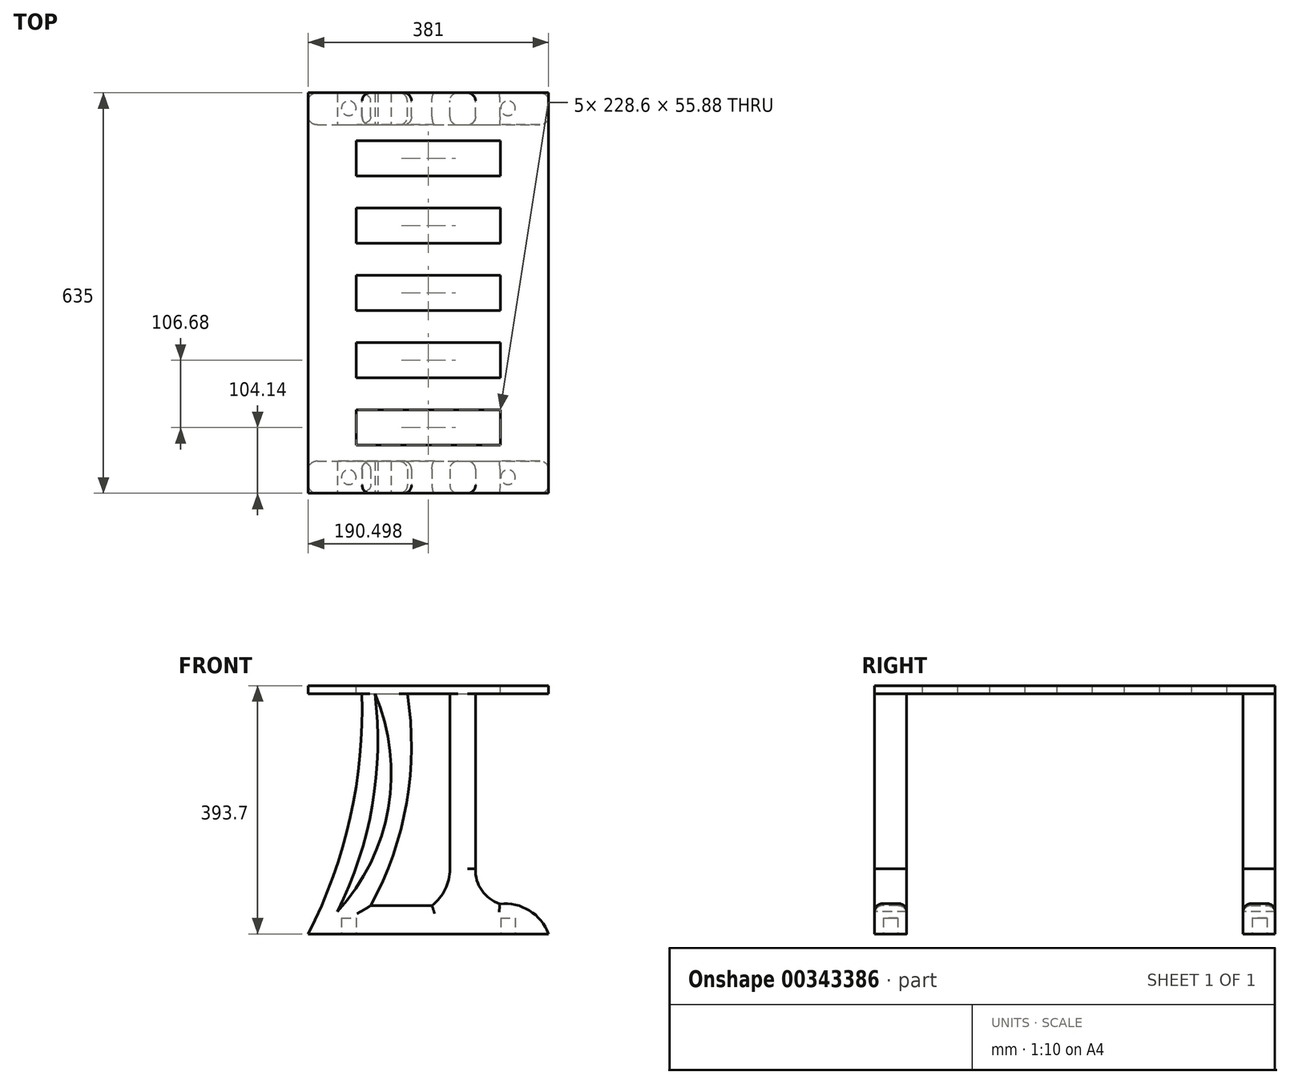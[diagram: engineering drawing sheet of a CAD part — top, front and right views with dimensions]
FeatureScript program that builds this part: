
annotation { "Feature Type Name" : "Feature", "Feature Type Description" : "" }
export const myFeature = defineFeature(function(context is Context, id is Id, definition is map)
    precondition{}
    {
        {
            var Q0;
            Q0=qCreatedBy(makeId("Front.planeOp"),FACE);
            var sketch = newSketch(context, id + "F0", { "sketchPlane" : qUnion([Q0])});
            skArc(sketch, "E0", {"start": v(156.47, -381) * mm, "mid": v(126, -343.99) * mm, "end": v(79.24, -333.37) * mm});
            skArc(sketch, "E1", {"start": v(40.62, -278.03) * mm, "mid": v(50.62, -312.2) * mm, "end": v(79.24, -333.37) * mm});
            skLineSegment(sketch, "E2", {"start": v(40.62, -278.03) * mm, "end": v(40.62, 0) * mm});
            skLineSegment(sketch, "E3", {"start": v(0, 0) * mm, "end": v(0, -278.03) * mm});
            skArc(sketch, "E4", {"start": v(-28.4, -336.03) * mm, "mid": v(-7.48, -310.31) * mm, "end": v(0, -278.03) * mm});
            skArc(sketch, "E5", {"start": v(-224.53, -381) * mm, "mid": v(-157.8, -195.9) * mm, "end": v(-139.58, 0) * mm});
            skLineSegment(sketch, "E6", {"start": v(-224.53, -381) * mm, "end": v(156.47, -381) * mm});
            skLineSegment(sketch, "E7", {"start": v(-139.58, 0) * mm, "end": v(-67.5, 0) * mm});
            skLineSegment(sketch, "E8", {"start": v(0, 0) * mm, "end": v(40.62, 0) * mm});
            skArc(sketch, "E9", {"start": v(-125.38, -336.03) * mm, "mid": v(-68.53, -172.82) * mm, "end": v(-67.5, 0) * mm});
            skLineSegment(sketch, "E10", {"start": v(-28.4, -336.03) * mm, "end": v(-125.38, -336.03) * mm});
            skSolve(sketch);
        }
        {
            var Q0;
            Q0=makeQuery(id+"F0.imprint","IMPRINT",FACE,{"disambiguationData":[TD([[makeQuery(id+"F0.imprint","IMPRINT",EDGE,{"derivedFrom":sQuery(id+"F0.wireOp",EDGE,"E0")}),1.0]])]});
            extrude(context, id + "F1", {"entities" : qUnion([Q0]), "depth" : 50.8 * mm});
        }
        {
            var Q0;
            Q0=qCreatedBy(makeId("Front.planeOp"),FACE);
            var sketch = newSketch(context, id + "F2", { "sketchPlane" : qUnion([Q0])});
            skLineSegment(sketch, "E11", {"start": v(-224.53, 0) * mm, "end": v(156.47, 0) * mm});
            skLineSegment(sketch, "E12", {"start": v(-224.53, 0) * mm, "end": v(-224.53, 12.7) * mm});
            skLineSegment(sketch, "E13", {"start": v(-224.53, 12.7) * mm, "end": v(156.47, 12.7) * mm});
            skLineSegment(sketch, "E14", {"start": v(156.47, 12.7) * mm, "end": v(156.47, 0) * mm});
            skSolve(sketch);
        }
        {
            var Q0;
            Q0=makeQuery(id+"F2.imprint","IMPRINT",FACE,{"disambiguationData":[TD([[makeQuery(id+"F2.imprint","IMPRINT",EDGE,{"derivedFrom":sQuery(id+"F2.wireOp",EDGE,"E11")}),1.0]])]});
            extrude(context, id + "F3", {"entities" : qUnion([Q0]), "operationType" : NewBodyOperationType.ADD, "depth" : 317.5 * mm});
        }
        {
            var Q0;
            Q0=makeQuery(id+"F1.opExtrude","CAP_EDGE",EDGE,{"disambiguationData":[OSD([sQuery(id+"F0.wireOp",EDGE,"E1")])],"isStart":true});
            var Q1;
            Q1=makeQuery(id+"F1.opExtrude","CAP_EDGE",EDGE,{"disambiguationData":[OSD([sQuery(id+"F0.wireOp",EDGE,"E1")])],"isStart":false});
            var Q2;
            Q2=makeQuery(id+"F1.opExtrude","CAP_EDGE",EDGE,{"disambiguationData":[OSD([sQuery(id+"F0.wireOp",EDGE,"E0")])],"isStart":true});
            var Q3;
            Q3=makeQuery(id+"F1.opExtrude","CAP_EDGE",EDGE,{"disambiguationData":[OSD([sQuery(id+"F0.wireOp",EDGE,"E0")])],"isStart":false});
            var Q4;
            Q4=makeQuery(id+"F1.opExtrude","CAP_EDGE",EDGE,{"disambiguationData":[OSD([sQuery(id+"F0.wireOp",EDGE,"E2")])],"isStart":true});
            var Q5;
            Q5=makeQuery(id+"F1.opExtrude","CAP_EDGE",EDGE,{"disambiguationData":[OSD([sQuery(id+"F0.wireOp",EDGE,"E2")])],"isStart":false});
            fillet(context, id + "F4", {"entities" : qUnion([Q0, Q1, Q2, Q3, Q4, Q5]), "radius" : 12.7 * mm, "tangentPropagation" : true, "allowEdgeOverflow" : false});
        }
        {
            var Q0;
            Q0=makeQuery(id+"F1.opExtrude","CAP_EDGE",EDGE,{"disambiguationData":[OSD([sQuery(id+"F0.wireOp",EDGE,"E3")])],"isStart":true});
            var Q1;
            Q1=makeQuery(id+"F1.opExtrude","CAP_EDGE",EDGE,{"disambiguationData":[OSD([sQuery(id+"F0.wireOp",EDGE,"E3")])],"isStart":false});
            var Q2;
            Q2=makeQuery(id+"F1.opExtrude","CAP_EDGE",EDGE,{"disambiguationData":[OSD([sQuery(id+"F0.wireOp",EDGE,"E10")])],"isStart":false});
            var Q3;
            Q3=makeQuery(id+"F1.opExtrude","CAP_EDGE",EDGE,{"disambiguationData":[OSD([sQuery(id+"F0.wireOp",EDGE,"E10")])],"isStart":true});
            var Q4;
            Q4=makeQuery(id+"F1.opExtrude","CAP_EDGE",EDGE,{"disambiguationData":[OSD([sQuery(id+"F0.wireOp",EDGE,"E9")])],"isStart":true});
            var Q5;
            Q5=makeQuery(id+"F1.opExtrude","CAP_EDGE",EDGE,{"disambiguationData":[OSD([sQuery(id+"F0.wireOp",EDGE,"E9")])],"isStart":false});
            var Q6;
            Q6=makeQuery(id+"F1.opExtrude","CAP_EDGE",EDGE,{"disambiguationData":[OSD([sQuery(id+"F0.wireOp",EDGE,"E5")])],"isStart":false});
            var Q7;
            Q7=makeQuery(id+"F1.opExtrude","CAP_EDGE",EDGE,{"disambiguationData":[OSD([sQuery(id+"F0.wireOp",EDGE,"E5")])],"isStart":true});
            fillet(context, id + "F5", {"entities" : qUnion([Q0, Q1, Q2, Q3, Q4, Q5, Q6, Q7]), "radius" : 12.7 * mm, "tangentPropagation" : true, "allowEdgeOverflow" : false});
        }
        {
            var Q0;
            Q0=makeQuery(id+"F1.opExtrude","SWEPT_BODY",BODY,{"disambiguationData":[OSD([sQuery(id+"F0.wireOp",EDGE,"E0"),sQuery(id+"F0.wireOp",EDGE,"E1"),sQuery(id+"F0.wireOp",EDGE,"E2"),sQuery(id+"F0.wireOp",EDGE,"E3"),sQuery(id+"F0.wireOp",EDGE,"E4"),sQuery(id+"F0.wireOp",EDGE,"E5"),sQuery(id+"F0.wireOp",EDGE,"E6"),sQuery(id+"F0.wireOp",EDGE,"E7"),sQuery(id+"F0.wireOp",EDGE,"E8"),sQuery(id+"F0.wireOp",EDGE,"E9"),sQuery(id+"F0.wireOp",EDGE,"E10")])]});
            var Q1;
            Q1=makeQuery(id+"F3.opExtrude","CAP_FACE",FACE,{"disambiguationData":[OSD([sQuery(id+"F2.wireOp",EDGE,"E11"),sQuery(id+"F2.wireOp",EDGE,"E12"),sQuery(id+"F2.wireOp",EDGE,"E13"),sQuery(id+"F2.wireOp",EDGE,"E14")])],"isStart":false});
            mirror(context, id + "F6", {"operationType" : NewBodyOperationType.ADD, "entities" : qUnion([Q0]), "mirrorPlane" : qUnion([Q1])});
        }
        {
            var Q0;
            Q0=makeQuery(id+"F6.opPattern","COPY",FACE,{"derivedFrom":makeQuery(id+"F1.opExtrude","SWEPT_FACE",FACE,{"disambiguationData":[OSD([sQuery(id+"F0.wireOp",EDGE,"E6")])]}),"instanceName":"1"});
            var sketch = newSketch(context, id + "F7", { "sketchPlane" : qUnion([Q0])});
            skCircle(sketch, "E15", {"center": v(-160.3, 24.41) * mm, "radius": 11.57 * mm});
            skCircle(sketch, "E16", {"center": v(92.12, 24.41) * mm, "radius": 11.57 * mm});
            skCircle(sketch, "E17", {"center": v(-160.3, 609.6) * mm, "radius": 11.57 * mm});
            skCircle(sketch, "E18", {"center": v(92.12, 609.6) * mm, "radius": 11.57 * mm});
            skSolve(sketch);
        }
        {
            var Q0;
            Q0=makeQuery(id+"F7.imprint","IMPRINT",FACE,{"disambiguationData":[TD([[makeQuery(id+"F7.imprint","IMPRINT",EDGE,{"derivedFrom":sQuery(id+"F7.wireOp",EDGE,"E17")}),1.0]])]});
            var Q1;
            Q1=makeQuery(id+"F7.imprint","IMPRINT",FACE,{"disambiguationData":[TD([[makeQuery(id+"F7.imprint","IMPRINT",EDGE,{"derivedFrom":sQuery(id+"F7.wireOp",EDGE,"E18")}),1.0]])]});
            var Q2;
            Q2=makeQuery(id+"F7.imprint","IMPRINT",FACE,{"disambiguationData":[TD([[makeQuery(id+"F7.imprint","IMPRINT",EDGE,{"derivedFrom":sQuery(id+"F7.wireOp",EDGE,"E15")}),1.0]])]});
            var Q3;
            Q3=makeQuery(id+"F7.imprint","IMPRINT",FACE,{"disambiguationData":[TD([[makeQuery(id+"F7.imprint","IMPRINT",EDGE,{"derivedFrom":sQuery(id+"F7.wireOp",EDGE,"E16")}),1.0]])]});
            extrude(context, id + "F8", {"entities" : qUnion([Q0, Q1, Q2, Q3]), "operationType" : NewBodyOperationType.REMOVE, "oppositeDirection" : true, "depth" : 25.4 * mm});
        }
        {
            var Q0;
            Q0=makeQuery(id+"F6.opPattern","COPY",FACE,{"derivedFrom":makeQuery(id+"F3.boolean.opBoolean","MERGE",FACE,{"derivedFrom":[makeQuery(id+"F1.opExtrude","CAP_FACE",FACE,{"disambiguationData":[OSD([sQuery(id+"F0.wireOp",EDGE,"E0"),sQuery(id+"F0.wireOp",EDGE,"E1"),sQuery(id+"F0.wireOp",EDGE,"E2"),sQuery(id+"F0.wireOp",EDGE,"E3"),sQuery(id+"F0.wireOp",EDGE,"E4"),sQuery(id+"F0.wireOp",EDGE,"E5"),sQuery(id+"F0.wireOp",EDGE,"E6"),sQuery(id+"F0.wireOp",EDGE,"E7"),sQuery(id+"F0.wireOp",EDGE,"E8"),sQuery(id+"F0.wireOp",EDGE,"E9"),sQuery(id+"F0.wireOp",EDGE,"E10")])],"isStart":true}),makeQuery(id+"F3.opExtrude","CAP_FACE",FACE,{"disambiguationData":[OSD([sQuery(id+"F2.wireOp",EDGE,"E11"),sQuery(id+"F2.wireOp",EDGE,"E12"),sQuery(id+"F2.wireOp",EDGE,"E13"),sQuery(id+"F2.wireOp",EDGE,"E14")])],"isStart":true})]}),"instanceName":"1"});
            var sketch = newSketch(context, id + "F9", { "sketchPlane" : qUnion([Q0])});
            skArc(sketch, "E19", {"start": v(-178.6, -345.71) * mm, "mid": v(-123, -177.3) * mm, "end": v(-118.99, 0) * mm});
            skArc(sketch, "E20", {"start": v(-178.6, -345.71) * mm, "mid": v(-97.66, -181.67) * mm, "end": v(-118.99, 0) * mm});
            skSolve(sketch);
        }
        {
            var Q0;
            Q0=makeQuery(id+"F9.imprint","IMPRINT",FACE,{"disambiguationData":[TD([[makeQuery(id+"F9.imprint","IMPRINT",EDGE,{"derivedFrom":sQuery(id+"F9.wireOp",EDGE,"E19")}),-1.0]])]});
            extrude(context, id + "F10", {"entities" : qUnion([Q0]), "operationType" : NewBodyOperationType.REMOVE, "endBound" : BoundingType.THROUGH_ALL, "oppositeDirection" : true, "depth" : 25.4 * mm});
        }
        {
            var Q0;
            {var subQ0=makeQuery(id+"F3.opExtrude","SWEPT_FACE",FACE,{"disambiguationData":[OSD([sQuery(id+"F2.wireOp",EDGE,"E13")])]});Q0=makeQuery(id+"F6.boolean.opBoolean","MERGE",FACE,{"derivedFrom":[subQ0,makeQuery(id+"F6.opPattern","COPY",FACE,{"derivedFrom":subQ0,"instanceName":"1"})]});}
            var sketch = newSketch(context, id + "F11", { "sketchPlane" : qUnion([Q0])});
            skLineSegment(sketch, "E21.bottom", {"start": v(-148.33, -558.8) * mm, "end": v(80.27, -558.8) * mm});
            skLineSegment(sketch, "E21.top", {"start": v(-148.33, -502.92) * mm, "end": v(80.27, -502.92) * mm});
            skLineSegment(sketch, "E21.left", {"start": v(-148.33, -558.8) * mm, "end": v(-148.33, -502.92) * mm});
            skLineSegment(sketch, "E21.right", {"start": v(80.27, -558.8) * mm, "end": v(80.27, -502.92) * mm});
            skLineSegment(sketch, "E22.bottom", {"start": v(-148.33, -452.12) * mm, "end": v(80.27, -452.12) * mm});
            skLineSegment(sketch, "E22.top", {"start": v(-148.33, -396.24) * mm, "end": v(80.27, -396.24) * mm});
            skLineSegment(sketch, "E22.left", {"start": v(-148.33, -452.12) * mm, "end": v(-148.33, -396.24) * mm});
            skLineSegment(sketch, "E22.right", {"start": v(80.27, -452.12) * mm, "end": v(80.27, -396.24) * mm});
            skLineSegment(sketch, "E23.bottom", {"start": v(-148.33, -345.44) * mm, "end": v(80.27, -345.44) * mm});
            skLineSegment(sketch, "E23.top", {"start": v(-148.33, -289.56) * mm, "end": v(80.27, -289.56) * mm});
            skLineSegment(sketch, "E23.left", {"start": v(-148.33, -345.44) * mm, "end": v(-148.33, -289.56) * mm});
            skLineSegment(sketch, "E23.right", {"start": v(80.27, -345.44) * mm, "end": v(80.27, -289.56) * mm});
            skLineSegment(sketch, "E24.bottom", {"start": v(-148.33, -238.76) * mm, "end": v(80.27, -238.76) * mm});
            skLineSegment(sketch, "E24.top", {"start": v(-148.33, -76.2) * mm, "end": v(80.27, -76.2) * mm});
            skLineSegment(sketch, "E24.left", {"start": v(-148.33, -238.76) * mm, "end": v(-148.33, -182.88) * mm});
            skLineSegment(sketch, "E24.right", {"start": v(80.27, -238.76) * mm, "end": v(80.27, -182.88) * mm});
            skLineSegment(sketch, "E25", {"start": v(156.47, -635) * mm, "end": v(-224.53, -635) * mm});
            skLineSegment(sketch, "E26", {"start": v(156.47, 0) * mm, "end": v(-224.53, 0) * mm});
            skLineSegment(sketch, "E27", {"start": v(80.27, -182.88) * mm, "end": v(-148.33, -182.88) * mm});
            skLineSegment(sketch, "E28", {"start": v(80.27, -132.08) * mm, "end": v(-148.33, -132.08) * mm});
            skLineSegment(sketch, "E29.trimOffspring", {"start": v(-148.33, -132.08) * mm, "end": v(-148.33, -76.2) * mm});
            skLineSegment(sketch, "E30.trimOffspring", {"start": v(80.27, -132.08) * mm, "end": v(80.27, -76.2) * mm});
            skSolve(sketch);
        }
        {
            var Q0;
            Q0=makeQuery(id+"F11.imprint","IMPRINT",FACE,{"disambiguationData":[TD([[makeQuery(id+"F11.imprint","IMPRINT",EDGE,{"derivedFrom":sQuery(id+"F11.wireOp",EDGE,"E21.bottom")}),1.0]])]});
            var Q1;
            Q1=makeQuery(id+"F11.imprint","IMPRINT",FACE,{"disambiguationData":[TD([[makeQuery(id+"F11.imprint","IMPRINT",EDGE,{"derivedFrom":sQuery(id+"F11.wireOp",EDGE,"E22.bottom")}),1.0]])]});
            var Q2;
            Q2=makeQuery(id+"F11.imprint","IMPRINT",FACE,{"disambiguationData":[TD([[makeQuery(id+"F11.imprint","IMPRINT",EDGE,{"derivedFrom":sQuery(id+"F11.wireOp",EDGE,"E23.bottom")}),1.0]])]});
            var Q3;
            Q3=makeQuery(id+"F11.imprint","IMPRINT",FACE,{"disambiguationData":[TD([[makeQuery(id+"F11.imprint","IMPRINT",EDGE,{"derivedFrom":sQuery(id+"F11.wireOp",EDGE,"E24.bottom")}),1.0]])]});
            var Q4;
            Q4=makeQuery(id+"F11.imprint","IMPRINT",FACE,{"disambiguationData":[TD([[makeQuery(id+"F11.imprint","IMPRINT",EDGE,{"derivedFrom":sQuery(id+"F11.wireOp",EDGE,"E24.top")}),-1.0]])]});
            extrude(context, id + "F12", {"entities" : qUnion([Q0, Q1, Q2, Q3, Q4]), "operationType" : NewBodyOperationType.REMOVE, "endBound" : BoundingType.THROUGH_ALL, "oppositeDirection" : true, "depth" : 25.4 * mm});
        }
    });
